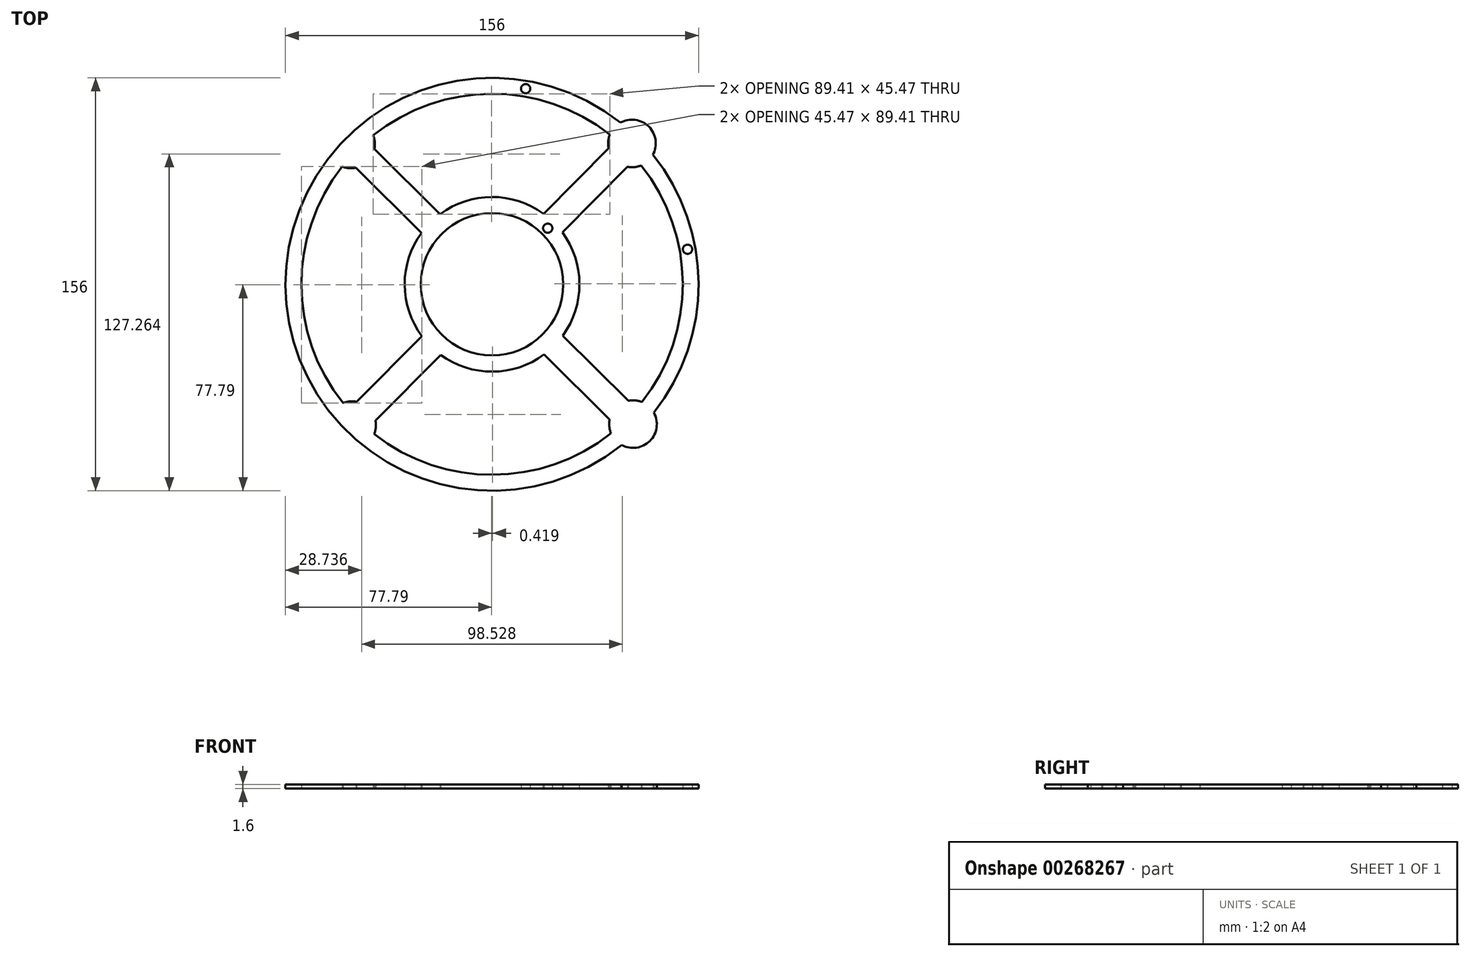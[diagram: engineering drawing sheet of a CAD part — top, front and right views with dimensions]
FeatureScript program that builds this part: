
annotation { "Feature Type Name" : "Feature", "Feature Type Description" : "" }
export const myFeature = defineFeature(function(context is Context, id is Id, definition is map)
    precondition{}
    {
        {
            assignVariable(context, id + "F0", {"name" : "plhi", "anyValue" : 1.6});
        }
        {
            var Q0;
            Q0=qCreatedBy(makeId("Top.planeOp"),FACE);
            var sketch = newSketch(context, id + "F1", { "sketchPlane" : qUnion([Q0])});
            skCircle(sketch, "E0", {"center": v(0, 0) * mm, "radius": 33 * mm});
            skCircle(sketch, "E1", {"center": v(0, 0) * mm, "radius": 75 * mm});
            skLineSegment(sketch, "E2", {"start": v(-100.94, -101.69) * mm, "end": v(100.94, 101.69) * mm, "construction": true});
            skLineSegment(sketch, "E3", {"start": v(100.94, -100.19) * mm, "end": v(-100.94, 100.19) * mm, "construction": true});
            skCircle(sketch, "E4", {"center": v(52.84, 53.23) * mm, "radius": 48.1 * mm});
            skCircle(sketch, "E5", {"center": v(53.23, -52.84) * mm, "radius": 48.1 * mm});
            skCircle(sketch, "E6", {"center": v(-52.84, -53.23) * mm, "radius": 48.1 * mm});
            skCircle(sketch, "E7", {"center": v(-53.23, 52.84) * mm, "radius": 48.1 * mm});
            skLineSegment(sketch, "E8", {"start": v(100.94, 101.69) * mm, "end": v(100.94, -100.19) * mm, "construction": true});
            skLineSegment(sketch, "E9", {"start": v(-100.94, 100.19) * mm, "end": v(-100.94, -101.69) * mm, "construction": true});
            skCircle(sketch, "E10", {"center": v(52.84, 53.23) * mm, "radius": 9 * mm});
            skLineSegment(sketch, "E11", {"start": v(44.02, 51.44) * mm, "end": v(19.43, 26.67) * mm});
            skLineSegment(sketch, "E12.MirrorCS", {"start": v(51.11, 44.4) * mm, "end": v(26.53, 19.63) * mm});
            skLineSegment(sketch, "E13.1.0", {"start": v(44.4, -51.11) * mm, "end": v(19.63, -26.53) * mm});
            skCircle(sketch, "E13.1.1", {"center": v(53.23, -52.84) * mm, "radius": 9 * mm});
            skLineSegment(sketch, "E13.1.2", {"start": v(51.44, -44.02) * mm, "end": v(26.67, -19.43) * mm});
            skLineSegment(sketch, "E13.2.0", {"start": v(-51.11, -44.4) * mm, "end": v(-26.53, -19.63) * mm});
            skCircle(sketch, "E13.2.1", {"center": v(-52.84, -53.23) * mm, "radius": 9 * mm});
            skLineSegment(sketch, "E13.2.2", {"start": v(-44.02, -51.44) * mm, "end": v(-19.43, -26.67) * mm});
            skLineSegment(sketch, "E13.3.0", {"start": v(-44.4, 51.11) * mm, "end": v(-19.63, 26.53) * mm});
            skCircle(sketch, "E13.3.1", {"center": v(-53.23, 52.84) * mm, "radius": 9 * mm});
            skLineSegment(sketch, "E13.3.2", {"start": v(-51.44, 44.02) * mm, "end": v(-26.67, 19.43) * mm});
            skLineSegment(sketch, "E13.anchor1", {"start": v(0, 0) * mm, "end": v(52.84, 53.23) * mm, "construction": true});
            skLineSegment(sketch, "E13.anchor2", {"start": v(0, 0) * mm, "end": v(-53.23, 52.84) * mm, "construction": true});
            skPoint(sketch, "E14", {"position": v(-10.19, 74.3) * mm});
            skPoint(sketch, "E15", {"position": v(9.63, 74.38) * mm});
            skCircle(sketch, "E16", {"center": v(52.84, 53.23) * mm, "radius": 38.1 * mm, "construction": true});
            skCircle(sketch, "E17.1.0", {"center": v(-53.23, 52.84) * mm, "radius": 38.1 * mm, "construction": true});
            skCircle(sketch, "E17.2.0", {"center": v(-52.84, -53.23) * mm, "radius": 38.1 * mm, "construction": true});
            skCircle(sketch, "E17.3.0", {"center": v(53.23, -52.84) * mm, "radius": 38.1 * mm, "construction": true});
            skCircle(sketch, "E18", {"center": v(0, 0) * mm, "radius": 26.9 * mm});
            skCircle(sketch, "E19.0", {"center": v(0, 0) * mm, "radius": 78 * mm});
            skCircle(sketch, "E20.0", {"center": v(0, 0) * mm, "radius": 72 * mm});
            skCircle(sketch, "E21", {"center": v(12.7, 73.92) * mm, "radius": 2.95 * mm});
            skCircle(sketch, "E22", {"center": v(12.7, 73.92) * mm, "radius": 1.75 * mm});
            skCircle(sketch, "E23.MirrorC", {"center": v(73.82, 13.25) * mm, "radius": 2.95 * mm});
            skCircle(sketch, "E24.MirrorC", {"center": v(73.82, 13.25) * mm, "radius": 1.75 * mm});
            skCircle(sketch, "E25", {"center": v(21.03, 21.19) * mm, "radius": 1.75 * mm});
            skCircle(sketch, "E26", {"center": v(21.03, 21.19) * mm, "radius": 2.95 * mm});
            skSolve(sketch);
        }
        {
            var Q0;
            {var subQ0=sQuery(id+"F1.wireOp",EDGE,"E13.3.0");var subQ1=sQuery(id+"F1.wireOp",EDGE,"E0");var subQ2=makeQuery(id+"F1.imprint","INTERSECT",VERTEX,{"derivedFrom":[subQ1,subQ0]});Q0=makeQuery(id+"F1.imprint","IMPRINT",FACE,{"disambiguationData":[TD([[makeQuery(id+"F1.imprint","IMPRINT",EDGE,{"disambiguationData":[TD([[subQ2,-1.0]])],"derivedFrom":subQ1}),-1.0]])]});}
            var Q1;
            {var subQ0=sQuery(id+"F1.wireOp",EDGE,"E10");var subQ1=sQuery(id+"F1.wireOp",EDGE,"E1");var subQ2=makeQuery(id+"F1.imprint","INTERSECT",VERTEX,{"disambiguationData":[OD(0.0)],"derivedFrom":[subQ1,subQ0]});Q1=makeQuery(id+"F1.imprint","IMPRINT",FACE,{"disambiguationData":[TD([[makeQuery(id+"F1.imprint","IMPRINT",EDGE,{"disambiguationData":[TD([[subQ2,-1.0]])],"derivedFrom":subQ1}),1.0]])]});}
            var Q2;
            {var subQ0=sQuery(id+"F1.wireOp",EDGE,"E10");var subQ1=sQuery(id+"F1.wireOp",EDGE,"E1");var subQ2=makeQuery(id+"F1.imprint","INTERSECT",VERTEX,{"disambiguationData":[OD(0.0)],"derivedFrom":[subQ1,subQ0]});Q2=makeQuery(id+"F1.imprint","IMPRINT",FACE,{"disambiguationData":[TD([[makeQuery(id+"F1.imprint","IMPRINT",EDGE,{"disambiguationData":[TD([[subQ2,-1.0]])],"derivedFrom":subQ1}),-1.0]])]});}
            var Q3;
            {var subQ0=sQuery(id+"F1.wireOp",EDGE,"E13.1.1");var subQ1=sQuery(id+"F1.wireOp",EDGE,"E1");var subQ2=makeQuery(id+"F1.imprint","INTERSECT",VERTEX,{"disambiguationData":[OD(0.0)],"derivedFrom":[subQ1,subQ0]});Q3=makeQuery(id+"F1.imprint","IMPRINT",FACE,{"disambiguationData":[TD([[makeQuery(id+"F1.imprint","IMPRINT",EDGE,{"disambiguationData":[TD([[subQ2,-1.0]])],"derivedFrom":subQ1}),1.0]])]});}
            var Q4;
            {var subQ0=sQuery(id+"F1.wireOp",EDGE,"E0");var subQ15=makeQuery(id+"F1.imprint","INTERSECT",VERTEX,{"derivedFrom":[subQ0,sQuery(id+"F1.wireOp",EDGE,"E12.MirrorCS")]});Q4=makeQuery(id+"F1.imprint","IMPRINT",FACE,{"disambiguationData":[TD([[makeQuery(id+"F1.imprint","IMPRINT",EDGE,{"disambiguationData":[TD([[subQ15,-1.0]])],"derivedFrom":subQ0}),1.0]])]});}
            var Q5;
            {var subQ0=sQuery(id+"F1.wireOp",EDGE,"E13.2.0");var subQ1=sQuery(id+"F1.wireOp",EDGE,"E0");var subQ2=makeQuery(id+"F1.imprint","INTERSECT",VERTEX,{"derivedFrom":[subQ1,subQ0]});Q5=makeQuery(id+"F1.imprint","IMPRINT",FACE,{"disambiguationData":[TD([[makeQuery(id+"F1.imprint","IMPRINT",EDGE,{"disambiguationData":[TD([[subQ2,-1.0]])],"derivedFrom":subQ1}),-1.0]])]});}
            var Q6;
            {var subQ0=sQuery(id+"F1.wireOp",EDGE,"E13.3.1");var subQ1=sQuery(id+"F1.wireOp",EDGE,"E1");var subQ2=makeQuery(id+"F1.imprint","INTERSECT",VERTEX,{"disambiguationData":[OD(0.0)],"derivedFrom":[subQ1,subQ0]});Q6=makeQuery(id+"F1.imprint","IMPRINT",FACE,{"disambiguationData":[TD([[makeQuery(id+"F1.imprint","IMPRINT",EDGE,{"disambiguationData":[TD([[subQ2,-1.0]])],"derivedFrom":subQ1}),1.0]])]});}
            var Q7;
            {var subQ0=sQuery(id+"F1.wireOp",EDGE,"E12.MirrorCS");var subQ1=sQuery(id+"F1.wireOp",EDGE,"E0");var subQ2=makeQuery(id+"F1.imprint","INTERSECT",VERTEX,{"derivedFrom":[subQ1,subQ0]});Q7=makeQuery(id+"F1.imprint","IMPRINT",FACE,{"disambiguationData":[TD([[makeQuery(id+"F1.imprint","IMPRINT",EDGE,{"disambiguationData":[TD([[subQ2,-1.0]])],"derivedFrom":subQ1}),-1.0]])]});}
            var Q8;
            {var subQ0=sQuery(id+"F1.wireOp",EDGE,"E13.2.1");var subQ1=sQuery(id+"F1.wireOp",EDGE,"E1");var subQ2=makeQuery(id+"F1.imprint","INTERSECT",VERTEX,{"disambiguationData":[OD(0.0)],"derivedFrom":[subQ1,subQ0]});Q8=makeQuery(id+"F1.imprint","IMPRINT",FACE,{"disambiguationData":[TD([[makeQuery(id+"F1.imprint","IMPRINT",EDGE,{"disambiguationData":[TD([[subQ2,-1.0]])],"derivedFrom":subQ1}),-1.0]])]});}
            var Q9;
            {var subQ0=sQuery(id+"F1.wireOp",EDGE,"E13.1.1");var subQ1=sQuery(id+"F1.wireOp",EDGE,"E1");var subQ2=makeQuery(id+"F1.imprint","INTERSECT",VERTEX,{"disambiguationData":[OD(0.0)],"derivedFrom":[subQ1,subQ0]});Q9=makeQuery(id+"F1.imprint","IMPRINT",FACE,{"disambiguationData":[TD([[makeQuery(id+"F1.imprint","IMPRINT",EDGE,{"disambiguationData":[TD([[subQ2,-1.0]])],"derivedFrom":subQ1}),-1.0]])]});}
            var Q10;
            {var subQ0=sQuery(id+"F1.wireOp",EDGE,"E13.1.0");var subQ1=sQuery(id+"F1.wireOp",EDGE,"E0");var subQ2=makeQuery(id+"F1.imprint","INTERSECT",VERTEX,{"derivedFrom":[subQ1,subQ0]});Q10=makeQuery(id+"F1.imprint","IMPRINT",FACE,{"disambiguationData":[TD([[makeQuery(id+"F1.imprint","IMPRINT",EDGE,{"disambiguationData":[TD([[subQ2,-1.0]])],"derivedFrom":subQ1}),-1.0]])]});}
            var Q11;
            {var subQ0=sQuery(id+"F1.wireOp",EDGE,"E13.1.2");var subQ1=sQuery(id+"F1.wireOp",EDGE,"E0");var subQ2=makeQuery(id+"F1.imprint","INTERSECT",VERTEX,{"derivedFrom":[subQ1,subQ0]});Q11=makeQuery(id+"F1.imprint","IMPRINT",FACE,{"disambiguationData":[TD([[makeQuery(id+"F1.imprint","IMPRINT",EDGE,{"disambiguationData":[TD([[subQ2,1.0]])],"derivedFrom":subQ1}),-1.0]])]});}
            var Q12;
            {var subQ0=sQuery(id+"F1.wireOp",EDGE,"E13.2.1");var subQ1=sQuery(id+"F1.wireOp",EDGE,"E1");var subQ2=makeQuery(id+"F1.imprint","INTERSECT",VERTEX,{"disambiguationData":[OD(0.0)],"derivedFrom":[subQ1,subQ0]});Q12=makeQuery(id+"F1.imprint","IMPRINT",FACE,{"disambiguationData":[TD([[makeQuery(id+"F1.imprint","IMPRINT",EDGE,{"disambiguationData":[TD([[subQ2,-1.0]])],"derivedFrom":subQ1}),1.0]])]});}
            var Q13;
            {var subQ0=sQuery(id+"F1.wireOp",EDGE,"E11");var subQ1=sQuery(id+"F1.wireOp",EDGE,"E0");var subQ2=makeQuery(id+"F1.imprint","INTERSECT",VERTEX,{"derivedFrom":[subQ1,subQ0]});Q13=makeQuery(id+"F1.imprint","IMPRINT",FACE,{"disambiguationData":[TD([[makeQuery(id+"F1.imprint","IMPRINT",EDGE,{"disambiguationData":[TD([[subQ2,1.0]])],"derivedFrom":subQ1}),-1.0]])]});}
            var Q14;
            {var subQ0=sQuery(id+"F1.wireOp",EDGE,"E13.3.2");var subQ1=sQuery(id+"F1.wireOp",EDGE,"E0");var subQ2=makeQuery(id+"F1.imprint","INTERSECT",VERTEX,{"derivedFrom":[subQ1,subQ0]});Q14=makeQuery(id+"F1.imprint","IMPRINT",FACE,{"disambiguationData":[TD([[makeQuery(id+"F1.imprint","IMPRINT",EDGE,{"disambiguationData":[TD([[subQ2,1.0]])],"derivedFrom":subQ1}),-1.0]])]});}
            var Q15;
            {var subQ0=sQuery(id+"F1.wireOp",EDGE,"E13.2.2");var subQ1=sQuery(id+"F1.wireOp",EDGE,"E0");var subQ2=makeQuery(id+"F1.imprint","INTERSECT",VERTEX,{"derivedFrom":[subQ1,subQ0]});Q15=makeQuery(id+"F1.imprint","IMPRINT",FACE,{"disambiguationData":[TD([[makeQuery(id+"F1.imprint","IMPRINT",EDGE,{"disambiguationData":[TD([[subQ2,1.0]])],"derivedFrom":subQ1}),-1.0]])]});}
            var Q16;
            {var subQ0=sQuery(id+"F1.wireOp",EDGE,"E13.3.1");var subQ1=sQuery(id+"F1.wireOp",EDGE,"E1");var subQ2=makeQuery(id+"F1.imprint","INTERSECT",VERTEX,{"disambiguationData":[OD(0.0)],"derivedFrom":[subQ1,subQ0]});Q16=makeQuery(id+"F1.imprint","IMPRINT",FACE,{"disambiguationData":[TD([[makeQuery(id+"F1.imprint","IMPRINT",EDGE,{"disambiguationData":[TD([[subQ2,-1.0]])],"derivedFrom":subQ1}),-1.0]])]});}
            var Q17;
            {var subQ0=sQuery(id+"F1.wireOp",EDGE,"E4");var subQ1=sQuery(id+"F1.wireOp",EDGE,"E0");var subQ2=makeQuery(id+"F1.imprint","INTERSECT",VERTEX,{"disambiguationData":[OD(0.0)],"derivedFrom":[subQ1,subQ0]});Q17=makeQuery(id+"F1.imprint","IMPRINT",FACE,{"disambiguationData":[TD([[makeQuery(id+"F1.imprint","IMPRINT",EDGE,{"disambiguationData":[TD([[subQ2,-1.0]])],"derivedFrom":subQ1}),1.0]])]});}
            var Q18;
            {var subQ0=sQuery(id+"F1.wireOp",EDGE,"E7");var subQ1=sQuery(id+"F1.wireOp",EDGE,"E0");var subQ2=makeQuery(id+"F1.imprint","INTERSECT",VERTEX,{"disambiguationData":[OD(0.0)],"derivedFrom":[subQ1,subQ0]});Q18=makeQuery(id+"F1.imprint","IMPRINT",FACE,{"disambiguationData":[TD([[makeQuery(id+"F1.imprint","IMPRINT",EDGE,{"disambiguationData":[TD([[subQ2,-1.0]])],"derivedFrom":subQ1}),1.0]])]});}
            var Q19;
            {var subQ0=sQuery(id+"F1.wireOp",EDGE,"E6");var subQ1=sQuery(id+"F1.wireOp",EDGE,"E0");var subQ2=makeQuery(id+"F1.imprint","INTERSECT",VERTEX,{"disambiguationData":[OD(0.0)],"derivedFrom":[subQ1,subQ0]});Q19=makeQuery(id+"F1.imprint","IMPRINT",FACE,{"disambiguationData":[TD([[makeQuery(id+"F1.imprint","IMPRINT",EDGE,{"disambiguationData":[TD([[subQ2,-1.0]])],"derivedFrom":subQ1}),1.0]])]});}
            var Q20;
            {var subQ0=sQuery(id+"F1.wireOp",EDGE,"E5");var subQ1=sQuery(id+"F1.wireOp",EDGE,"E0");var subQ2=makeQuery(id+"F1.imprint","INTERSECT",VERTEX,{"disambiguationData":[OD(0.0)],"derivedFrom":[subQ1,subQ0]});Q20=makeQuery(id+"F1.imprint","IMPRINT",FACE,{"disambiguationData":[TD([[makeQuery(id+"F1.imprint","IMPRINT",EDGE,{"disambiguationData":[TD([[subQ2,-1.0]])],"derivedFrom":subQ1}),1.0]])]});}
            var Q21;
            {var subQ0=sQuery(id+"F1.wireOp",EDGE,"E4");var subQ1=sQuery(id+"F1.wireOp",EDGE,"E0");var subQ11=makeQuery(id+"F1.imprint","INTERSECT",VERTEX,{"disambiguationData":[OD(1.0)],"derivedFrom":[subQ1,subQ0]});Q21=makeQuery(id+"F1.imprint","IMPRINT",FACE,{"disambiguationData":[TD([[makeQuery(id+"F1.imprint","IMPRINT",EDGE,{"disambiguationData":[TD([[subQ11,-1.0]])],"derivedFrom":subQ1}),1.0]])]});}
            var Q22;
            {var subQ0=sQuery(id+"F1.wireOp",EDGE,"E4");var subQ1=sQuery(id+"F1.wireOp",EDGE,"E0");var subQ2=makeQuery(id+"F1.imprint","INTERSECT",VERTEX,{"disambiguationData":[OD(0.0)],"derivedFrom":[subQ1,subQ0]});Q22=makeQuery(id+"F1.imprint","IMPRINT",FACE,{"disambiguationData":[TD([[makeQuery(id+"F1.imprint","IMPRINT",EDGE,{"disambiguationData":[TD([[subQ2,1.0]])],"derivedFrom":subQ1}),1.0]])]});}
            var Q23;
            {var subQ0=sQuery(id+"F1.wireOp",EDGE,"E6");var subQ1=sQuery(id+"F1.wireOp",EDGE,"E0");var subQ2=makeQuery(id+"F1.imprint","INTERSECT",VERTEX,{"disambiguationData":[OD(1.0)],"derivedFrom":[subQ1,subQ0]});Q23=makeQuery(id+"F1.imprint","IMPRINT",FACE,{"disambiguationData":[TD([[makeQuery(id+"F1.imprint","IMPRINT",EDGE,{"disambiguationData":[TD([[subQ2,-1.0]])],"derivedFrom":subQ1}),1.0]])]});}
            var Q24;
            {var subQ0=sQuery(id+"F1.wireOp",EDGE,"E7");var subQ1=sQuery(id+"F1.wireOp",EDGE,"E0");var subQ2=makeQuery(id+"F1.imprint","INTERSECT",VERTEX,{"disambiguationData":[OD(1.0)],"derivedFrom":[subQ1,subQ0]});Q24=makeQuery(id+"F1.imprint","IMPRINT",FACE,{"disambiguationData":[TD([[makeQuery(id+"F1.imprint","IMPRINT",EDGE,{"disambiguationData":[TD([[subQ2,-1.0]])],"derivedFrom":subQ1}),1.0]])]});}
            var Q25;
            {var subQ0=sQuery(id+"F1.wireOp",EDGE,"E10");var subQ1=makeQuery(id+"F1.imprint","INTERSECT",VERTEX,{"derivedFrom":[subQ0,sQuery(id+"F1.wireOp",EDGE,"E11")]});Q25=makeQuery(id+"F1.imprint","IMPRINT",FACE,{"disambiguationData":[TD([[makeQuery(id+"F1.imprint","IMPRINT",EDGE,{"disambiguationData":[TD([[subQ1,1.0]])],"derivedFrom":subQ0}),1.0]])]});}
            var Q26;
            {var subQ0=sQuery(id+"F1.wireOp",EDGE,"E19.0");var subQ1=sQuery(id+"F1.wireOp",EDGE,"E10");var subQ2=makeQuery(id+"F1.imprint","INTERSECT",VERTEX,{"disambiguationData":[OD(0.0)],"derivedFrom":[subQ1,subQ0]});Q26=makeQuery(id+"F1.imprint","IMPRINT",FACE,{"disambiguationData":[TD([[makeQuery(id+"F1.imprint","IMPRINT",EDGE,{"disambiguationData":[TD([[subQ2,1.0]])],"derivedFrom":subQ1}),1.0]])]});}
            var Q27;
            {var subQ0=sQuery(id+"F1.wireOp",EDGE,"E10");var subQ1=sQuery(id+"F1.wireOp",EDGE,"E1");var subQ2=makeQuery(id+"F1.imprint","INTERSECT",VERTEX,{"disambiguationData":[OD(1.0)],"derivedFrom":[subQ1,subQ0]});Q27=makeQuery(id+"F1.imprint","IMPRINT",FACE,{"disambiguationData":[TD([[makeQuery(id+"F1.imprint","IMPRINT",EDGE,{"disambiguationData":[TD([[subQ2,-1.0]])],"derivedFrom":subQ1}),1.0]])]});}
            var Q28;
            {var subQ0=sQuery(id+"F1.wireOp",EDGE,"E10");var subQ1=sQuery(id+"F1.wireOp",EDGE,"E1");var subQ2=makeQuery(id+"F1.imprint","INTERSECT",VERTEX,{"disambiguationData":[OD(1.0)],"derivedFrom":[subQ1,subQ0]});Q28=makeQuery(id+"F1.imprint","IMPRINT",FACE,{"disambiguationData":[TD([[makeQuery(id+"F1.imprint","IMPRINT",EDGE,{"disambiguationData":[TD([[subQ2,-1.0]])],"derivedFrom":subQ1}),-1.0]])]});}
            var Q29;
            {var subQ0=sQuery(id+"F1.wireOp",EDGE,"E4");var subQ1=sQuery(id+"F1.wireOp",EDGE,"E1");var subQ2=makeQuery(id+"F1.imprint","INTERSECT",VERTEX,{"disambiguationData":[OD(1.0)],"derivedFrom":[subQ1,subQ0]});Q29=makeQuery(id+"F1.imprint","IMPRINT",FACE,{"disambiguationData":[TD([[makeQuery(id+"F1.imprint","IMPRINT",EDGE,{"disambiguationData":[TD([[subQ2,-1.0]])],"derivedFrom":subQ1}),1.0]])]});}
            var Q30;
            {var subQ0=sQuery(id+"F1.wireOp",EDGE,"E7");var subQ1=sQuery(id+"F1.wireOp",EDGE,"E1");var subQ2=makeQuery(id+"F1.imprint","INTERSECT",VERTEX,{"disambiguationData":[OD(0.0)],"derivedFrom":[subQ1,subQ0]});Q30=makeQuery(id+"F1.imprint","IMPRINT",FACE,{"disambiguationData":[TD([[makeQuery(id+"F1.imprint","IMPRINT",EDGE,{"disambiguationData":[TD([[subQ2,-1.0]])],"derivedFrom":subQ1}),1.0]])]});}
            var Q31;
            {var subQ0=sQuery(id+"F1.wireOp",EDGE,"E7");var subQ1=sQuery(id+"F1.wireOp",EDGE,"E1");var subQ2=makeQuery(id+"F1.imprint","INTERSECT",VERTEX,{"disambiguationData":[OD(0.0)],"derivedFrom":[subQ1,subQ0]});Q31=makeQuery(id+"F1.imprint","IMPRINT",FACE,{"disambiguationData":[TD([[makeQuery(id+"F1.imprint","IMPRINT",EDGE,{"disambiguationData":[TD([[subQ2,-1.0]])],"derivedFrom":subQ1}),-1.0]])]});}
            var Q32;
            {var subQ0=sQuery(id+"F1.wireOp",EDGE,"E13.3.1");var subQ1=makeQuery(id+"F1.imprint","INTERSECT",VERTEX,{"derivedFrom":[subQ0,sQuery(id+"F1.wireOp",EDGE,"E13.3.2")]});Q32=makeQuery(id+"F1.imprint","IMPRINT",FACE,{"disambiguationData":[TD([[makeQuery(id+"F1.imprint","IMPRINT",EDGE,{"disambiguationData":[TD([[subQ1,1.0]])],"derivedFrom":subQ0}),1.0]])]});}
            var Q33;
            {var subQ0=sQuery(id+"F1.wireOp",EDGE,"E19.0");var subQ1=sQuery(id+"F1.wireOp",EDGE,"E13.3.1");var subQ2=makeQuery(id+"F1.imprint","INTERSECT",VERTEX,{"disambiguationData":[OD(0.0)],"derivedFrom":[subQ1,subQ0]});Q33=makeQuery(id+"F1.imprint","IMPRINT",FACE,{"disambiguationData":[TD([[makeQuery(id+"F1.imprint","IMPRINT",EDGE,{"disambiguationData":[TD([[subQ2,1.0]])],"derivedFrom":subQ1}),1.0]])]});}
            var Q34;
            {var subQ0=sQuery(id+"F1.wireOp",EDGE,"E13.3.1");var subQ1=sQuery(id+"F1.wireOp",EDGE,"E1");var subQ2=makeQuery(id+"F1.imprint","INTERSECT",VERTEX,{"disambiguationData":[OD(1.0)],"derivedFrom":[subQ1,subQ0]});Q34=makeQuery(id+"F1.imprint","IMPRINT",FACE,{"disambiguationData":[TD([[makeQuery(id+"F1.imprint","IMPRINT",EDGE,{"disambiguationData":[TD([[subQ2,-1.0]])],"derivedFrom":subQ1}),-1.0]])]});}
            var Q35;
            {var subQ0=sQuery(id+"F1.wireOp",EDGE,"E13.3.1");var subQ1=sQuery(id+"F1.wireOp",EDGE,"E1");var subQ2=makeQuery(id+"F1.imprint","INTERSECT",VERTEX,{"disambiguationData":[OD(1.0)],"derivedFrom":[subQ1,subQ0]});Q35=makeQuery(id+"F1.imprint","IMPRINT",FACE,{"disambiguationData":[TD([[makeQuery(id+"F1.imprint","IMPRINT",EDGE,{"disambiguationData":[TD([[subQ2,-1.0]])],"derivedFrom":subQ1}),1.0]])]});}
            var Q36;
            {var subQ0=sQuery(id+"F1.wireOp",EDGE,"E7");var subQ1=sQuery(id+"F1.wireOp",EDGE,"E1");var subQ2=makeQuery(id+"F1.imprint","INTERSECT",VERTEX,{"disambiguationData":[OD(1.0)],"derivedFrom":[subQ1,subQ0]});Q36=makeQuery(id+"F1.imprint","IMPRINT",FACE,{"disambiguationData":[TD([[makeQuery(id+"F1.imprint","IMPRINT",EDGE,{"disambiguationData":[TD([[subQ2,-1.0]])],"derivedFrom":subQ1}),1.0]])]});}
            var Q37;
            {var subQ0=sQuery(id+"F1.wireOp",EDGE,"E7");var subQ1=sQuery(id+"F1.wireOp",EDGE,"E1");var subQ2=makeQuery(id+"F1.imprint","INTERSECT",VERTEX,{"disambiguationData":[OD(1.0)],"derivedFrom":[subQ1,subQ0]});Q37=makeQuery(id+"F1.imprint","IMPRINT",FACE,{"disambiguationData":[TD([[makeQuery(id+"F1.imprint","IMPRINT",EDGE,{"disambiguationData":[TD([[subQ2,-1.0]])],"derivedFrom":subQ1}),-1.0]])]});}
            var Q38;
            {var subQ0=sQuery(id+"F1.wireOp",EDGE,"E6");var subQ1=sQuery(id+"F1.wireOp",EDGE,"E1");var subQ2=makeQuery(id+"F1.imprint","INTERSECT",VERTEX,{"disambiguationData":[OD(0.0)],"derivedFrom":[subQ1,subQ0]});Q38=makeQuery(id+"F1.imprint","IMPRINT",FACE,{"disambiguationData":[TD([[makeQuery(id+"F1.imprint","IMPRINT",EDGE,{"disambiguationData":[TD([[subQ2,-1.0]])],"derivedFrom":subQ1}),-1.0]])]});}
            var Q39;
            {var subQ0=sQuery(id+"F1.wireOp",EDGE,"E6");var subQ1=sQuery(id+"F1.wireOp",EDGE,"E1");var subQ2=makeQuery(id+"F1.imprint","INTERSECT",VERTEX,{"disambiguationData":[OD(0.0)],"derivedFrom":[subQ1,subQ0]});Q39=makeQuery(id+"F1.imprint","IMPRINT",FACE,{"disambiguationData":[TD([[makeQuery(id+"F1.imprint","IMPRINT",EDGE,{"disambiguationData":[TD([[subQ2,-1.0]])],"derivedFrom":subQ1}),1.0]])]});}
            var Q40;
            {var subQ0=sQuery(id+"F1.wireOp",EDGE,"E13.2.1");var subQ1=makeQuery(id+"F1.imprint","INTERSECT",VERTEX,{"derivedFrom":[subQ0,sQuery(id+"F1.wireOp",EDGE,"E13.2.2")]});Q40=makeQuery(id+"F1.imprint","IMPRINT",FACE,{"disambiguationData":[TD([[makeQuery(id+"F1.imprint","IMPRINT",EDGE,{"disambiguationData":[TD([[subQ1,1.0]])],"derivedFrom":subQ0}),1.0]])]});}
            var Q41;
            {var subQ0=sQuery(id+"F1.wireOp",EDGE,"E19.0");var subQ1=sQuery(id+"F1.wireOp",EDGE,"E13.2.1");var subQ2=makeQuery(id+"F1.imprint","INTERSECT",VERTEX,{"disambiguationData":[OD(0.0)],"derivedFrom":[subQ1,subQ0]});Q41=makeQuery(id+"F1.imprint","IMPRINT",FACE,{"disambiguationData":[TD([[makeQuery(id+"F1.imprint","IMPRINT",EDGE,{"disambiguationData":[TD([[subQ2,1.0]])],"derivedFrom":subQ1}),1.0]])]});}
            var Q42;
            {var subQ0=sQuery(id+"F1.wireOp",EDGE,"E13.2.1");var subQ1=sQuery(id+"F1.wireOp",EDGE,"E1");var subQ2=makeQuery(id+"F1.imprint","INTERSECT",VERTEX,{"disambiguationData":[OD(1.0)],"derivedFrom":[subQ1,subQ0]});Q42=makeQuery(id+"F1.imprint","IMPRINT",FACE,{"disambiguationData":[TD([[makeQuery(id+"F1.imprint","IMPRINT",EDGE,{"disambiguationData":[TD([[subQ2,-1.0]])],"derivedFrom":subQ1}),-1.0]])]});}
            var Q43;
            {var subQ0=sQuery(id+"F1.wireOp",EDGE,"E13.2.1");var subQ1=sQuery(id+"F1.wireOp",EDGE,"E1");var subQ2=makeQuery(id+"F1.imprint","INTERSECT",VERTEX,{"disambiguationData":[OD(1.0)],"derivedFrom":[subQ1,subQ0]});Q43=makeQuery(id+"F1.imprint","IMPRINT",FACE,{"disambiguationData":[TD([[makeQuery(id+"F1.imprint","IMPRINT",EDGE,{"disambiguationData":[TD([[subQ2,-1.0]])],"derivedFrom":subQ1}),1.0]])]});}
            var Q44;
            {var subQ0=sQuery(id+"F1.wireOp",EDGE,"E6");var subQ1=sQuery(id+"F1.wireOp",EDGE,"E1");var subQ2=makeQuery(id+"F1.imprint","INTERSECT",VERTEX,{"disambiguationData":[OD(1.0)],"derivedFrom":[subQ1,subQ0]});Q44=makeQuery(id+"F1.imprint","IMPRINT",FACE,{"disambiguationData":[TD([[makeQuery(id+"F1.imprint","IMPRINT",EDGE,{"disambiguationData":[TD([[subQ2,-1.0]])],"derivedFrom":subQ1}),1.0]])]});}
            var Q45;
            {var subQ0=sQuery(id+"F1.wireOp",EDGE,"E6");var subQ1=sQuery(id+"F1.wireOp",EDGE,"E1");var subQ2=makeQuery(id+"F1.imprint","INTERSECT",VERTEX,{"disambiguationData":[OD(1.0)],"derivedFrom":[subQ1,subQ0]});Q45=makeQuery(id+"F1.imprint","IMPRINT",FACE,{"disambiguationData":[TD([[makeQuery(id+"F1.imprint","IMPRINT",EDGE,{"disambiguationData":[TD([[subQ2,-1.0]])],"derivedFrom":subQ1}),-1.0]])]});}
            var Q46;
            {var subQ0=sQuery(id+"F1.wireOp",EDGE,"E5");var subQ1=sQuery(id+"F1.wireOp",EDGE,"E1");var subQ2=makeQuery(id+"F1.imprint","INTERSECT",VERTEX,{"disambiguationData":[OD(0.0)],"derivedFrom":[subQ1,subQ0]});Q46=makeQuery(id+"F1.imprint","IMPRINT",FACE,{"disambiguationData":[TD([[makeQuery(id+"F1.imprint","IMPRINT",EDGE,{"disambiguationData":[TD([[subQ2,-1.0]])],"derivedFrom":subQ1}),-1.0]])]});}
            var Q47;
            {var subQ0=sQuery(id+"F1.wireOp",EDGE,"E5");var subQ1=sQuery(id+"F1.wireOp",EDGE,"E1");var subQ2=makeQuery(id+"F1.imprint","INTERSECT",VERTEX,{"disambiguationData":[OD(0.0)],"derivedFrom":[subQ1,subQ0]});Q47=makeQuery(id+"F1.imprint","IMPRINT",FACE,{"disambiguationData":[TD([[makeQuery(id+"F1.imprint","IMPRINT",EDGE,{"disambiguationData":[TD([[subQ2,-1.0]])],"derivedFrom":subQ1}),1.0]])]});}
            var Q48;
            {var subQ0=sQuery(id+"F1.wireOp",EDGE,"E13.1.1");var subQ1=makeQuery(id+"F1.imprint","INTERSECT",VERTEX,{"derivedFrom":[subQ0,sQuery(id+"F1.wireOp",EDGE,"E13.1.2")]});Q48=makeQuery(id+"F1.imprint","IMPRINT",FACE,{"disambiguationData":[TD([[makeQuery(id+"F1.imprint","IMPRINT",EDGE,{"disambiguationData":[TD([[subQ1,1.0]])],"derivedFrom":subQ0}),1.0]])]});}
            var Q49;
            {var subQ0=sQuery(id+"F1.wireOp",EDGE,"E19.0");var subQ1=sQuery(id+"F1.wireOp",EDGE,"E13.1.1");var subQ2=makeQuery(id+"F1.imprint","INTERSECT",VERTEX,{"disambiguationData":[OD(0.0)],"derivedFrom":[subQ1,subQ0]});Q49=makeQuery(id+"F1.imprint","IMPRINT",FACE,{"disambiguationData":[TD([[makeQuery(id+"F1.imprint","IMPRINT",EDGE,{"disambiguationData":[TD([[subQ2,1.0]])],"derivedFrom":subQ1}),1.0]])]});}
            var Q50;
            {var subQ0=sQuery(id+"F1.wireOp",EDGE,"E13.1.1");var subQ1=sQuery(id+"F1.wireOp",EDGE,"E1");var subQ2=makeQuery(id+"F1.imprint","INTERSECT",VERTEX,{"disambiguationData":[OD(1.0)],"derivedFrom":[subQ1,subQ0]});Q50=makeQuery(id+"F1.imprint","IMPRINT",FACE,{"disambiguationData":[TD([[makeQuery(id+"F1.imprint","IMPRINT",EDGE,{"disambiguationData":[TD([[subQ2,-1.0]])],"derivedFrom":subQ1}),-1.0]])]});}
            var Q51;
            {var subQ0=sQuery(id+"F1.wireOp",EDGE,"E13.1.1");var subQ1=sQuery(id+"F1.wireOp",EDGE,"E1");var subQ2=makeQuery(id+"F1.imprint","INTERSECT",VERTEX,{"disambiguationData":[OD(1.0)],"derivedFrom":[subQ1,subQ0]});Q51=makeQuery(id+"F1.imprint","IMPRINT",FACE,{"disambiguationData":[TD([[makeQuery(id+"F1.imprint","IMPRINT",EDGE,{"disambiguationData":[TD([[subQ2,-1.0]])],"derivedFrom":subQ1}),1.0]])]});}
            var Q52;
            {var subQ0=sQuery(id+"F1.wireOp",EDGE,"E4");var subQ1=sQuery(id+"F1.wireOp",EDGE,"E1");var subQ2=makeQuery(id+"F1.imprint","INTERSECT",VERTEX,{"disambiguationData":[OD(0.0)],"derivedFrom":[subQ1,subQ0]});Q52=makeQuery(id+"F1.imprint","IMPRINT",FACE,{"disambiguationData":[TD([[makeQuery(id+"F1.imprint","IMPRINT",EDGE,{"disambiguationData":[TD([[subQ2,1.0]])],"derivedFrom":subQ1}),1.0]])]});}
            var Q53;
            {var subQ0=sQuery(id+"F1.wireOp",EDGE,"E10");var subQ1=sQuery(id+"F1.wireOp",EDGE,"E1");var subQ2=makeQuery(id+"F1.imprint","INTERSECT",VERTEX,{"disambiguationData":[OD(0.0)],"derivedFrom":[subQ1,subQ0]});Q53=makeQuery(id+"F1.imprint","IMPRINT",FACE,{"disambiguationData":[TD([[makeQuery(id+"F1.imprint","IMPRINT",EDGE,{"disambiguationData":[TD([[subQ2,1.0]])],"derivedFrom":subQ1}),1.0]])]});}
            var Q54;
            {var subQ0=sQuery(id+"F1.wireOp",EDGE,"E10");var subQ1=sQuery(id+"F1.wireOp",EDGE,"E1");var subQ2=makeQuery(id+"F1.imprint","INTERSECT",VERTEX,{"disambiguationData":[OD(0.0)],"derivedFrom":[subQ1,subQ0]});Q54=makeQuery(id+"F1.imprint","IMPRINT",FACE,{"disambiguationData":[TD([[makeQuery(id+"F1.imprint","IMPRINT",EDGE,{"disambiguationData":[TD([[subQ2,1.0]])],"derivedFrom":subQ1}),-1.0]])]});}
            var Q55;
            {var subQ1=sQuery(id+"F1.wireOp",EDGE,"E1");var subQ4=sQuery(id+"F1.wireOp",EDGE,"E21");var subQ7=makeQuery(id+"F1.imprint","INTERSECT",VERTEX,{"disambiguationData":[OD(0.0)],"derivedFrom":[subQ1,subQ4]});Q55=makeQuery(id+"F1.imprint","IMPRINT",FACE,{"disambiguationData":[TD([[makeQuery(id+"F1.imprint","IMPRINT",EDGE,{"disambiguationData":[TD([[subQ7,-1.0]])],"derivedFrom":subQ1}),-1.0]])]});}
            var Q56;
            {var subQ0=sQuery(id+"F1.wireOp",EDGE,"E21");var subQ1=sQuery(id+"F1.wireOp",EDGE,"E1");var subQ2=makeQuery(id+"F1.imprint","INTERSECT",VERTEX,{"disambiguationData":[OD(0.0)],"derivedFrom":[subQ1,subQ0]});Q56=makeQuery(id+"F1.imprint","IMPRINT",FACE,{"disambiguationData":[TD([[makeQuery(id+"F1.imprint","IMPRINT",EDGE,{"disambiguationData":[TD([[subQ2,-1.0]])],"derivedFrom":subQ1}),1.0]])]});}
            var Q57;
            {var subQ0=sQuery(id+"F1.wireOp",EDGE,"E23.MirrorC");var subQ1=sQuery(id+"F1.wireOp",EDGE,"E1");var subQ4=makeQuery(id+"F1.imprint","INTERSECT",VERTEX,{"disambiguationData":[OD(0.0)],"derivedFrom":[subQ1,subQ0]});Q57=makeQuery(id+"F1.imprint","IMPRINT",FACE,{"disambiguationData":[TD([[makeQuery(id+"F1.imprint","IMPRINT",EDGE,{"disambiguationData":[TD([[subQ4,-1.0]])],"derivedFrom":subQ1}),-1.0]])]});}
            var Q58;
            {var subQ0=sQuery(id+"F1.wireOp",EDGE,"E23.MirrorC");var subQ1=sQuery(id+"F1.wireOp",EDGE,"E1");var subQ2=makeQuery(id+"F1.imprint","INTERSECT",VERTEX,{"disambiguationData":[OD(0.0)],"derivedFrom":[subQ1,subQ0]});Q58=makeQuery(id+"F1.imprint","IMPRINT",FACE,{"disambiguationData":[TD([[makeQuery(id+"F1.imprint","IMPRINT",EDGE,{"disambiguationData":[TD([[subQ2,-1.0]])],"derivedFrom":subQ1}),1.0]])]});}
            var Q59;
            {var subQ3=sQuery(id+"F1.wireOp",EDGE,"E1");var subQ5=sQuery(id+"F1.wireOp",EDGE,"E4");var subQ8=makeQuery(id+"F1.imprint","INTERSECT",VERTEX,{"disambiguationData":[OD(0.0)],"derivedFrom":[subQ3,subQ5]});Q59=makeQuery(id+"F1.imprint","IMPRINT",FACE,{"disambiguationData":[TD([[makeQuery(id+"F1.imprint","IMPRINT",EDGE,{"disambiguationData":[TD([[subQ8,1.0]])],"derivedFrom":subQ3}),-1.0]])]});}
            var Q60;
            {var subQ0=sQuery(id+"F1.wireOp",EDGE,"E23.MirrorC");var subQ1=sQuery(id+"F1.wireOp",EDGE,"E1");var subQ2=makeQuery(id+"F1.imprint","INTERSECT",VERTEX,{"disambiguationData":[OD(0.0)],"derivedFrom":[subQ1,subQ0]});Q60=makeQuery(id+"F1.imprint","IMPRINT",FACE,{"disambiguationData":[TD([[makeQuery(id+"F1.imprint","IMPRINT",EDGE,{"disambiguationData":[TD([[subQ2,1.0]])],"derivedFrom":subQ1}),-1.0]])]});}
            var Q61;
            {var subQ0=sQuery(id+"F1.wireOp",EDGE,"E21");var subQ1=sQuery(id+"F1.wireOp",EDGE,"E1");var subQ2=makeQuery(id+"F1.imprint","INTERSECT",VERTEX,{"disambiguationData":[OD(1.0)],"derivedFrom":[subQ1,subQ0]});Q61=makeQuery(id+"F1.imprint","IMPRINT",FACE,{"disambiguationData":[TD([[makeQuery(id+"F1.imprint","IMPRINT",EDGE,{"disambiguationData":[TD([[subQ2,-1.0]])],"derivedFrom":subQ1}),-1.0]])]});}
            var Q62;
            {var subQ3=sQuery(id+"F1.wireOp",EDGE,"E1");var subQ5=sQuery(id+"F1.wireOp",EDGE,"E4");var subQ6=makeQuery(id+"F1.imprint","INTERSECT",VERTEX,{"disambiguationData":[OD(1.0)],"derivedFrom":[subQ3,subQ5]});Q62=makeQuery(id+"F1.imprint","IMPRINT",FACE,{"disambiguationData":[TD([[makeQuery(id+"F1.imprint","IMPRINT",EDGE,{"disambiguationData":[TD([[subQ6,-1.0]])],"derivedFrom":subQ3}),-1.0]])]});}
            var Q63;
            Q63=makeQuery(id+"F1.imprint","IMPRINT",FACE,{"disambiguationData":[TD([[makeQuery(id+"F1.imprint","IMPRINT",EDGE,{"derivedFrom":sQuery(id+"F1.wireOp",EDGE,"E25")}),-1.0]])]});
            extrude(context, id + "F2", {"entities" : qUnion([Q0, Q1, Q2, Q3, Q4, Q5, Q6, Q7, Q8, Q9, Q10, Q11, Q12, Q13, Q14, Q15, Q16, Q17, Q18, Q19, Q20, Q21, Q22, Q23, Q24, Q25, Q26, Q27, Q28, Q29, Q30, Q31, Q32, Q33, Q34, Q35, Q36, Q37, Q38, Q39, Q40, Q41, Q42, Q43, Q44, Q45, Q46, Q47, Q48, Q49, Q50, Q51, Q52, Q53, Q54, Q55, Q56, Q57, Q58, Q59, Q60, Q61, Q62, Q63]), "depth" : (getVariable(context, 'plhi')) * mm});
        }
    });
